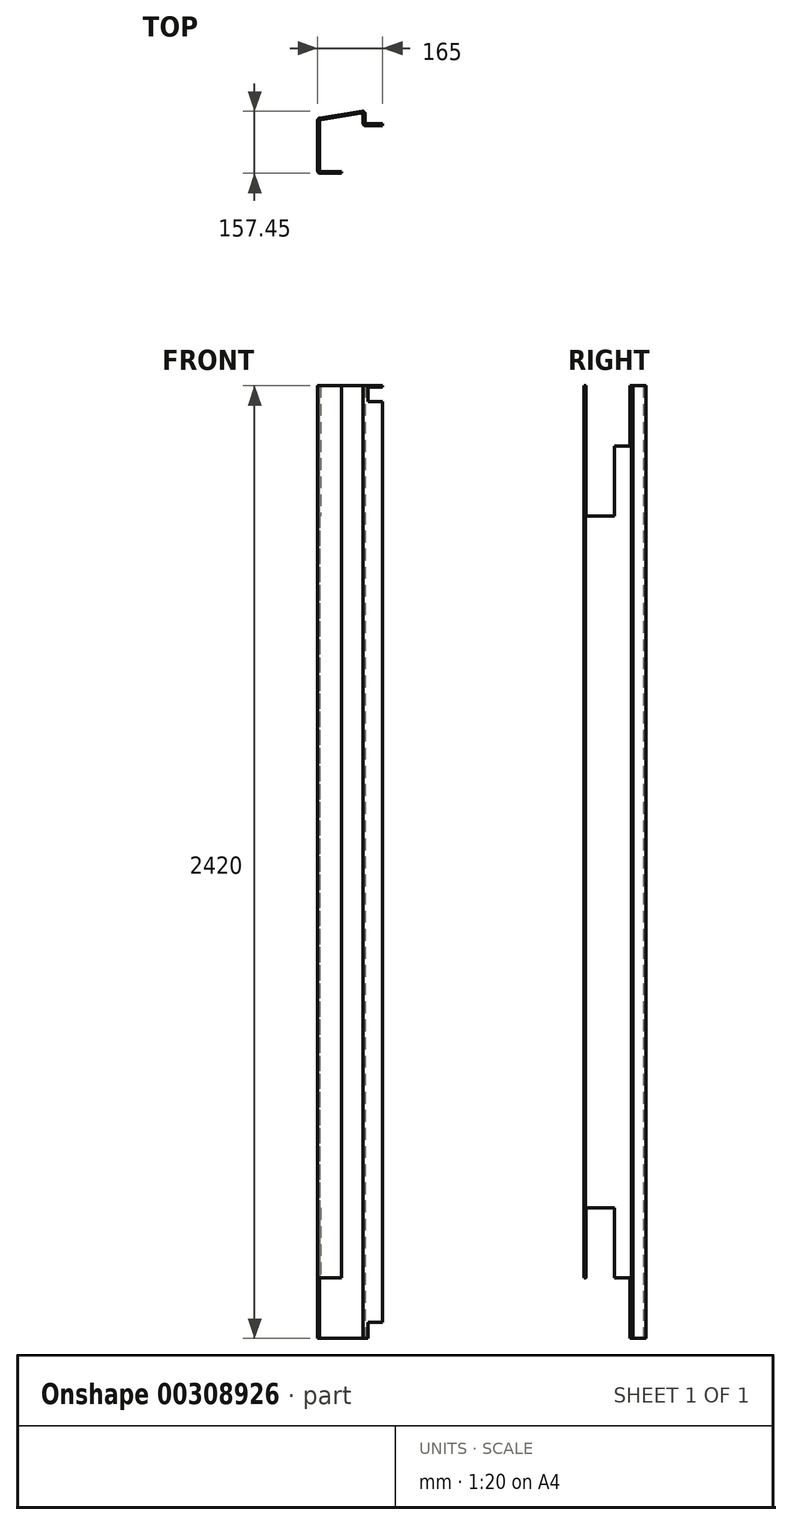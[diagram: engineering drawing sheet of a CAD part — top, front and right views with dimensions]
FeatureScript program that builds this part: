
annotation { "Feature Type Name" : "Feature", "Feature Type Description" : "" }
export const myFeature = defineFeature(function(context is Context, id is Id, definition is map)
    precondition{}
    {
        {
            var Q0;
            Q0=qCreatedBy(makeId("Top.planeOp"),FACE);
            var sketch = newSketch(context, id + "F0", { "sketchPlane" : qUnion([Q0])});
            skLineSegment(sketch, "E0", {"start": v(0, 0) * mm, "end": v(-54, 0) * mm});
            skLineSegment(sketch, "E1", {"start": v(-60, 0) * mm, "end": v(-60, 158.47) * mm, "construction": true});
            skLineSegment(sketch, "E2", {"start": v(-60, 158.47) * mm, "end": v(60, 158.47) * mm, "construction": true});
            skLineSegment(sketch, "E3", {"start": v(53.07, 157.38) * mm, "end": v(-54.93, 140.4) * mm});
            skLineSegment(sketch, "E4", {"start": v(60, 151.45) * mm, "end": v(60, 131.5) * mm});
            skLineSegment(sketch, "E5", {"start": v(66, 125.5) * mm, "end": v(105, 125.5) * mm});
            skLineSegment(sketch, "E6", {"start": v(-60, 134.48) * mm, "end": v(-60, 6) * mm});
            skLineSegment(sketch, "E7.0", {"start": v(61.5, 121) * mm, "end": v(105, 121) * mm});
            skLineSegment(sketch, "E7.1", {"start": v(0, 4.5) * mm, "end": v(-49.5, 4.5) * mm});
            skLineSegment(sketch, "E7.2", {"start": v(-55.5, 130.63) * mm, "end": v(-55.5, 10.5) * mm});
            skLineSegment(sketch, "E7.3", {"start": v(48.57, 152.12) * mm, "end": v(-50.43, 136.56) * mm});
            skLineSegment(sketch, "E7.4", {"start": v(55.5, 146.19) * mm, "end": v(55.5, 127) * mm});
            skLineSegment(sketch, "E8", {"start": v(0, 0) * mm, "end": v(0, 4.5) * mm});
            skLineSegment(sketch, "E9", {"start": v(105, 125.5) * mm, "end": v(105, 121) * mm});
            skPoint(sketch, "E10.visualSharp", {"position": v(-55.5, 4.5) * mm});
            skArc(sketch, "E10.filletArc", {"start": v(-55.5, 10.5) * mm, "mid": v(-53.74, 6.26) * mm, "end": v(-49.5, 4.5) * mm});
            skPoint(sketch, "E11.visualSharp", {"position": v(-60, 0) * mm});
            skArc(sketch, "E11.filletArc", {"start": v(-60, 6) * mm, "mid": v(-58.24, 1.76) * mm, "end": v(-54, 0) * mm});
            skPoint(sketch, "E12.visualSharp", {"position": v(-60, 139.6) * mm});
            skArc(sketch, "E12.filletArc", {"start": v(-54.93, 140.4) * mm, "mid": v(-58.56, 138.38) * mm, "end": v(-60, 134.48) * mm});
            skPoint(sketch, "E13.visualSharp", {"position": v(-55.5, 135.76) * mm});
            skArc(sketch, "E13.filletArc", {"start": v(-50.43, 136.56) * mm, "mid": v(-54.06, 134.53) * mm, "end": v(-55.5, 130.63) * mm});
            skPoint(sketch, "E14.visualSharp", {"position": v(55.5, 153.2) * mm});
            skArc(sketch, "E14.filletArc", {"start": v(55.5, 146.19) * mm, "mid": v(53.4, 150.75) * mm, "end": v(48.57, 152.12) * mm});
            skPoint(sketch, "E15.visualSharp", {"position": v(60, 158.47) * mm});
            skArc(sketch, "E15.filletArc", {"start": v(60, 151.45) * mm, "mid": v(57.9, 156.01) * mm, "end": v(53.07, 157.38) * mm});
            skPoint(sketch, "E16.visualSharp", {"position": v(60, 125.5) * mm});
            skArc(sketch, "E16.filletArc", {"start": v(60, 131.5) * mm, "mid": v(61.76, 127.26) * mm, "end": v(66, 125.5) * mm});
            skPoint(sketch, "E17.visualSharp", {"position": v(55.5, 121) * mm});
            skArc(sketch, "E17.filletArc", {"start": v(55.5, 127) * mm, "mid": v(57.26, 122.76) * mm, "end": v(61.5, 121) * mm});
            skSolve(sketch);
        }
        {
            var Q0;
            Q0=qSketchRegion(id+"F0",true);
            extrude(context, id + "F1", {"entities" : qUnion([Q0]), "depth" : 2420 * mm});
        }
        {
            var Q0;
            Q0=makeQuery(id+"F1.opExtrude","SWEPT_FACE",FACE,{"disambiguationData":[OSD([sQuery(id+"F0.wireOp",EDGE,"E6")])]});
            var sketch = newSketch(context, id + "F2", { "sketchPlane" : qUnion([Q0])});
            skLineSegment(sketch, "E18.bottom", {"start": v(-117.5, 0) * mm, "end": v(0, 0) * mm});
            skLineSegment(sketch, "E18.top", {"start": v(-117.5, 153) * mm, "end": v(0, 153) * mm});
            skLineSegment(sketch, "E18.left", {"start": v(-117.5, 0) * mm, "end": v(-117.5, 153) * mm});
            skLineSegment(sketch, "E18.right", {"start": v(0, 0) * mm, "end": v(0, 153) * mm});
            skLineSegment(sketch, "E19.0", {"start": v(0, 2420) * mm, "end": v(0, 0) * mm});
            skLineSegment(sketch, "E20.bottom", {"start": v(0, 153) * mm, "end": v(-78, 153) * mm});
            skLineSegment(sketch, "E20.top", {"start": v(0, 331) * mm, "end": v(-78, 331) * mm});
            skLineSegment(sketch, "E20.left", {"start": v(0, 153) * mm, "end": v(0, 331) * mm});
            skLineSegment(sketch, "E20.right", {"start": v(-78, 153) * mm, "end": v(-78, 331) * mm});
            skLineSegment(sketch, "E21", {"start": v(-6, 1210) * mm, "end": v(-364.7, 1210) * mm});
            skLineSegment(sketch, "E22.MirrorCS", {"start": v(-117.5, 2267) * mm, "end": v(0, 2267) * mm});
            skLineSegment(sketch, "E23.MirrorCS", {"start": v(0, 2420) * mm, "end": v(0, 2267) * mm});
            skLineSegment(sketch, "E24.MirrorCS", {"start": v(0, 2267) * mm, "end": v(-78, 2267) * mm});
            skLineSegment(sketch, "E25.MirrorCS", {"start": v(-78, 2267) * mm, "end": v(-78, 2089) * mm});
            skLineSegment(sketch, "E26.MirrorCS", {"start": v(-117.5, 2420) * mm, "end": v(0, 2420) * mm});
            skLineSegment(sketch, "E27.MirrorCS", {"start": v(-117.5, 2420) * mm, "end": v(-117.5, 2267) * mm});
            skLineSegment(sketch, "E28.MirrorCS", {"start": v(0, 2089) * mm, "end": v(-78, 2089) * mm});
            skLineSegment(sketch, "E29.MirrorCS", {"start": v(0, 2267) * mm, "end": v(0, 2089) * mm});
            skSolve(sketch);
        }
        {
            var Q0;
            {var subQ2=sQuery(id+"F2.wireOp",EDGE,"E18.top");Q0=makeQuery(id+"F2.imprint","IMPRINT",FACE,{"disambiguationData":[TD([[makeQuery(id+"F2.imprint","IMPRINT",EDGE,{"derivedFrom":subQ2}),-1.0]])]});}
            var Q1;
            {var subQ0=sQuery(id+"F2.wireOp",EDGE,"E18.bottom");var subQ3=sQuery(id+"F2.wireOp",EDGE,"E19.0");var subQ4=makeQuery(id+"F2.imprint","INTERSECT",VERTEX,{"derivedFrom":[subQ0,subQ3]});Q1=makeQuery(id+"F2.imprint","IMPRINT",FACE,{"disambiguationData":[TD([[makeQuery(id+"F2.imprint","IMPRINT",EDGE,{"disambiguationData":[TD([[subQ4,1.0]])],"derivedFrom":subQ0}),1.0]])]});}
            var Q2;
            {var subQ0=sQuery(id+"F2.wireOp",EDGE,"E20.right");Q2=makeQuery(id+"F2.imprint","IMPRINT",FACE,{"disambiguationData":[TD([[makeQuery(id+"F2.imprint","IMPRINT",EDGE,{"derivedFrom":subQ0}),-1.0]])]});}
            var Q3;
            {var subQ0=sQuery(id+"F2.wireOp",EDGE,"E20.left");Q3=makeQuery(id+"F2.imprint","IMPRINT",FACE,{"disambiguationData":[TD([[makeQuery(id+"F2.imprint","IMPRINT",EDGE,{"derivedFrom":subQ0}),1.0]])]});}
            var Q4;
            {var subQ0=sQuery(id+"F2.wireOp",EDGE,"E25.MirrorCS");Q4=makeQuery(id+"F2.imprint","IMPRINT",FACE,{"disambiguationData":[TD([[makeQuery(id+"F2.imprint","IMPRINT",EDGE,{"derivedFrom":subQ0}),1.0]])]});}
            var Q5;
            {var subQ0=sQuery(id+"F2.wireOp",EDGE,"E29.MirrorCS");Q5=makeQuery(id+"F2.imprint","IMPRINT",FACE,{"disambiguationData":[TD([[makeQuery(id+"F2.imprint","IMPRINT",EDGE,{"derivedFrom":subQ0}),-1.0]])]});}
            var Q6;
            {var subQ2=sQuery(id+"F2.wireOp",EDGE,"E22.MirrorCS");Q6=makeQuery(id+"F2.imprint","IMPRINT",FACE,{"disambiguationData":[TD([[makeQuery(id+"F2.imprint","IMPRINT",EDGE,{"derivedFrom":subQ2}),1.0]])]});}
            var Q7;
            {var subQ0=sQuery(id+"F2.wireOp",EDGE,"E23.MirrorCS");Q7=makeQuery(id+"F2.imprint","IMPRINT",FACE,{"disambiguationData":[TD([[makeQuery(id+"F2.imprint","IMPRINT",EDGE,{"derivedFrom":subQ0}),-1.0]])]});}
            extrude(context, id + "F3", {"entities" : qUnion([Q0, Q1, Q2, Q3, Q4, Q5, Q6, Q7]), "operationType" : NewBodyOperationType.REMOVE, "endBound" : BoundingType.THROUGH_ALL, "oppositeDirection" : true, "depth" : 25 * mm});
        }
        {
            var Q0;
            Q0=makeQuery(id+"F1.opExtrude","SWEPT_FACE",FACE,{"disambiguationData":[OSD([sQuery(id+"F0.wireOp",EDGE,"E5")])]});
            var sketch = newSketch(context, id + "F4", { "sketchPlane" : qUnion([Q0])});
            skLineSegment(sketch, "E30.left", {"start": v(-105, 0) * mm, "end": v(-105, 40) * mm});
            skLineSegment(sketch, "E31.bottom", {"start": v(-105, 40) * mm, "end": v(-67.5, 40) * mm});
            skLineSegment(sketch, "E31.top", {"start": v(-105, 0) * mm, "end": v(-67.5, 0) * mm});
            skLineSegment(sketch, "E31.left", {"start": v(-105, 40) * mm, "end": v(-105, 0) * mm});
            skLineSegment(sketch, "E31.right", {"start": v(-67.5, 40) * mm, "end": v(-67.5, 0) * mm});
            skLineSegment(sketch, "E32", {"start": v(-105, 1210) * mm, "end": v(-271.67, 1210) * mm});
            skLineSegment(sketch, "E33.MirrorCS", {"start": v(-105, 2420) * mm, "end": v(-105, 2380) * mm});
            skLineSegment(sketch, "E34.MirrorCS", {"start": v(-105, 2380) * mm, "end": v(-105, 2420) * mm});
            skLineSegment(sketch, "E35.MirrorCS", {"start": v(-67.5, 2380) * mm, "end": v(-67.5, 2420) * mm});
            skLineSegment(sketch, "E36.MirrorCS", {"start": v(-105, 2420) * mm, "end": v(-67.5, 2420) * mm});
            skLineSegment(sketch, "E37.MirrorCS", {"start": v(-105, 2380) * mm, "end": v(-67.5, 2380) * mm});
            skPoint(sketch, "E38", {"position": v(-67.5, 2417) * mm});
            skLineSegment(sketch, "E39.bottom", {"start": v(-67.5, 2417) * mm, "end": v(-105, 2417) * mm});
            skLineSegment(sketch, "E39.top", {"start": v(-67.5, 2377) * mm, "end": v(-105, 2377) * mm});
            skLineSegment(sketch, "E39.left", {"start": v(-67.5, 2417) * mm, "end": v(-67.5, 2377) * mm});
            skLineSegment(sketch, "E39.right", {"start": v(-105, 2417) * mm, "end": v(-105, 2377) * mm});
            skLineSegment(sketch, "E40.bottom", {"start": v(-67.5, 2417) * mm, "end": v(107.13, 2417) * mm});
            skLineSegment(sketch, "E40.top", {"start": v(-67.5, 2462.16) * mm, "end": v(107.13, 2462.16) * mm});
            skLineSegment(sketch, "E40.left", {"start": v(-67.5, 2417) * mm, "end": v(-67.5, 2462.16) * mm});
            skLineSegment(sketch, "E40.right", {"start": v(107.13, 2417) * mm, "end": v(107.13, 2462.16) * mm});
            skSolve(sketch);
        }
        {
            var Q0;
            {var subQ0=sQuery(id+"F4.wireOp",EDGE,"E37.MirrorCS");Q0=makeQuery(id+"F4.imprint","IMPRINT",FACE,{"disambiguationData":[TD([[makeQuery(id+"F4.imprint","IMPRINT",EDGE,{"derivedFrom":subQ0}),1.0]])]});}
            var Q1;
            Q1=makeQuery(id+"F4.imprint","IMPRINT",FACE,{"disambiguationData":[TD([[makeQuery(id+"F4.imprint","IMPRINT",EDGE,{"derivedFrom":sQuery(id+"F4.wireOp",EDGE,"E34.MirrorCS")}),1.0]])]});
            var Q2;
            Q2=makeQuery(id+"F4.imprint","IMPRINT",FACE,{"disambiguationData":[TD([[makeQuery(id+"F4.imprint","IMPRINT",EDGE,{"derivedFrom":sQuery(id+"F4.wireOp",EDGE,"E31.bottom")}),-1.0]])]});
            extrude(context, id + "F5", {"entities" : qUnion([Q0, Q1, Q2]), "operationType" : NewBodyOperationType.REMOVE, "endBound" : BoundingType.THROUGH_ALL, "oppositeDirection" : true, "depth" : 25 * mm});
        }
    });
